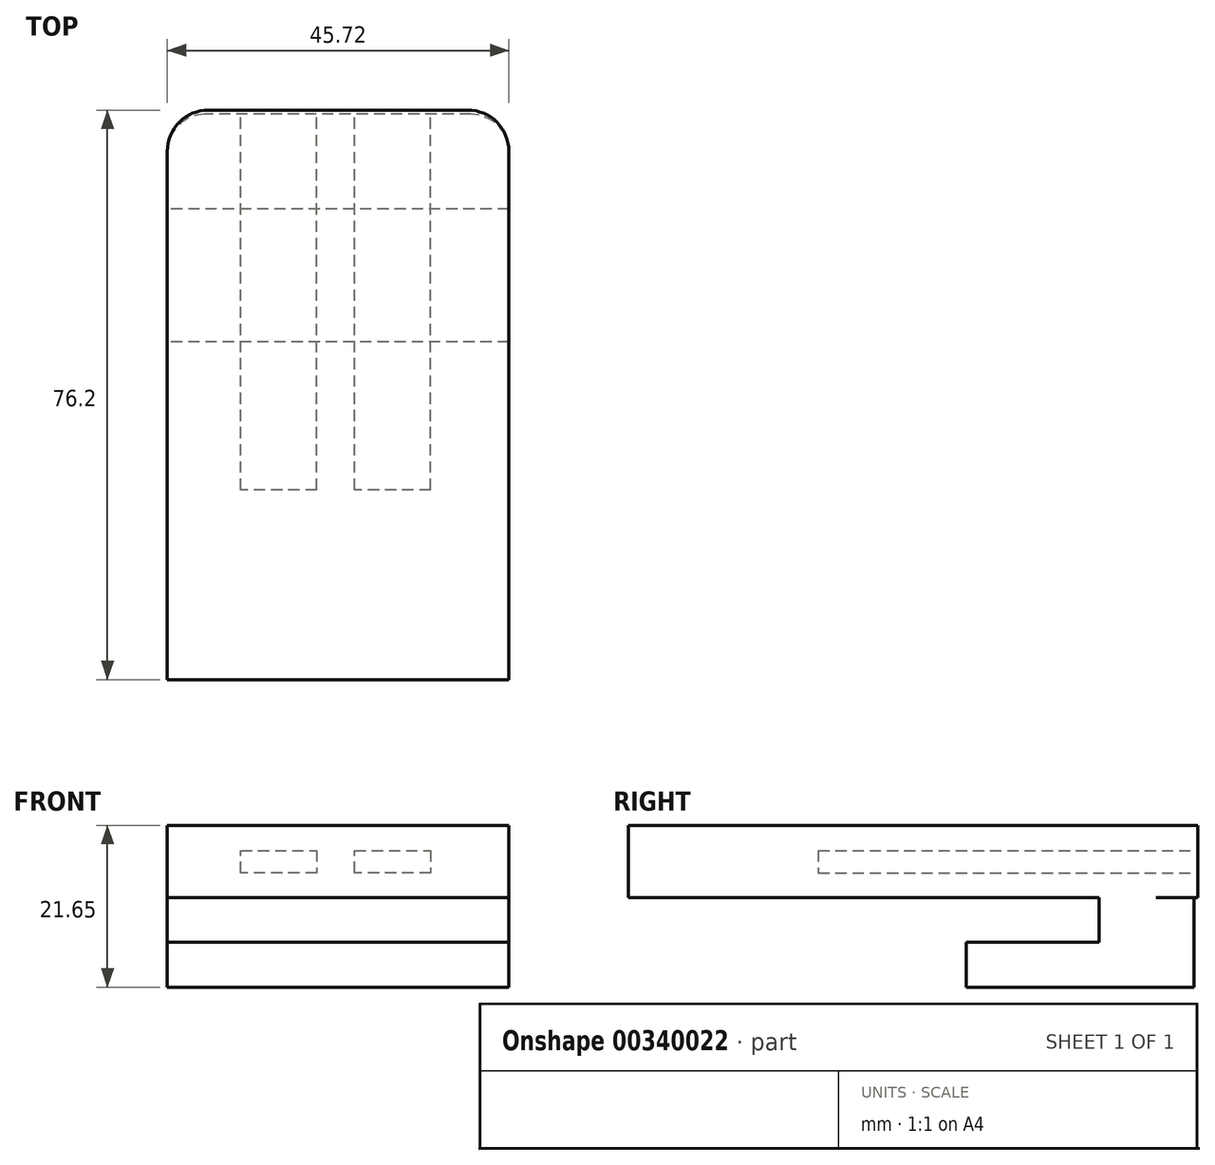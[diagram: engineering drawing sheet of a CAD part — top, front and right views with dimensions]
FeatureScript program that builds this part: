
annotation { "Feature Type Name" : "Feature", "Feature Type Description" : "" }
export const myFeature = defineFeature(function(context is Context, id is Id, definition is map)
    precondition{}
    {
        {
            var Q0;
            Q0=qCreatedBy(makeId("Top.planeOp"),FACE);
            var sketch = newSketch(context, id + "F0", { "sketchPlane" : qUnion([Q0])});
            skLineSegment(sketch, "E0", {"start": v(0, 0) * mm, "end": v(0, 13.65) * mm});
            skLineSegment(sketch, "E1", {"start": v(0, 0) * mm, "end": v(0, -62.55) * mm});
            skLineSegment(sketch, "E2", {"start": v(0, -62.55) * mm, "end": v(45.72, -62.55) * mm});
            skLineSegment(sketch, "E3", {"start": v(45.72, -62.55) * mm, "end": v(45.72, 13.65) * mm});
            skLineSegment(sketch, "E4", {"start": v(45.72, 13.65) * mm, "end": v(0, 13.65) * mm});
            skSolve(sketch);
        }
        {
            var Q0;
            Q0 = qSketchRegion(id + "F0", true);
            extrude(context, id + "F1", {"entities" : qUnion([Q0]), "depth" : 9.65 * mm});
        }
        {
            var Q0;
            Q0=qCreatedBy(makeId("Top.planeOp"),FACE);
            var sketch = newSketch(context, id + "F2", { "sketchPlane" : qUnion([Q0])});
            skLineSegment(sketch, "E5", {"start": v(0, 0) * mm, "end": v(0, 51.2) * mm});
            skLineSegment(sketch, "E6", {"start": v(0, 51.2) * mm, "end": v(0, -25) * mm});
            skLineSegment(sketch, "E7", {"start": v(0, -25) * mm, "end": v(45.72, -25) * mm});
            skLineSegment(sketch, "E8", {"start": v(45.72, -25) * mm, "end": v(45.72, 51.56) * mm});
            skLineSegment(sketch, "E9", {"start": v(45.72, 51.56) * mm, "end": v(0, 51.2) * mm});
            skSolve(sketch);
        }
        {
            var Q0;
            Q0=qCreatedBy(makeId("Right.planeOp"),FACE);
            var sketch = newSketch(context, id + "F3", { "sketchPlane" : qUnion([Q0])});
            skLineSegment(sketch, "E10", {"start": v(13.1, 0) * mm, "end": v(13.1, -12) * mm});
            skPoint(sketch, "E11.endSnap0", {"position": v(13.1, -6) * mm});
            skLineSegment(sketch, "E12", {"start": v(-17.38, -6) * mm, "end": v(0.4, -6) * mm});
            skLineSegment(sketch, "E13", {"start": v(0.4, -6) * mm, "end": v(0.4, 0) * mm});
            skLineSegment(sketch, "E14", {"start": v(13.1, 0) * mm, "end": v(0.4, 0) * mm});
            skLineSegment(sketch, "E15", {"start": v(13.1, -12) * mm, "end": v(-17.38, -12) * mm});
            skLineSegment(sketch, "E16", {"start": v(-17.38, -6) * mm, "end": v(-17.38, -12) * mm});
            skSolve(sketch);
        }
        {
            var Q0;
            Q0 = qSketchRegion(id + "F3", true);
            extrude(context, id + "F4", {"entities" : qUnion([Q0]), "operationType" : NewBodyOperationType.ADD, "depth" : 45.72 * mm});
        }
        {
            var Q0;
            Q0=makeQuery(id+"F4.opExtrude","CAP_EDGE",EDGE,{"disambiguationData":[OSD([sQuery(id+"F3.wireOp",EDGE,"E10")])],"isStart":false});
            var Q1;
            Q1=makeQuery(id+"F4.opExtrude","CAP_EDGE",EDGE,{"disambiguationData":[OSD([sQuery(id+"F3.wireOp",EDGE,"E10")])],"isStart":true});
            fillet(context, id + "F5", {"entities" : qUnion([Q0, Q1]), "radius" : 5.08 * mm, "tangentPropagation" : true, "allowEdgeOverflow" : false});
        }
        {
            var Q0;
            Q0=makeQuery(id+"F1.opExtrude","SWEPT_EDGE",EDGE,{"disambiguationData":[OSD([sQuery(id+"F0.wireOp",EDGE,"E3"),sQuery(id+"F0.wireOp",EDGE,"E4")])]});
            var Q1;
            Q1=makeQuery(id+"F1.opExtrude","SWEPT_EDGE",EDGE,{"disambiguationData":[OSD([sQuery(id+"F0.wireOp",EDGE,"E0"),sQuery(id+"F0.wireOp",EDGE,"E4")])]});
            fillet(context, id + "F6", {"entities" : qUnion([Q0, Q1]), "radius" : 5.52 * mm, "tangentPropagation" : true, "allowEdgeOverflow" : false});
        }
        {
            var Q0;
            Q0=makeQuery(id+"F1.opExtrude","SWEPT_FACE",FACE,{"disambiguationData":[OSD([sQuery(id+"F0.wireOp",EDGE,"E4")])]});
            var sketch = newSketch(context, id + "F7", { "sketchPlane" : qUnion([Q0])});
            skLineSegment(sketch, "E17", {"start": v(-35.24, 3.28) * mm, "end": v(-25.08, 3.28) * mm});
            skLineSegment(sketch, "E18", {"start": v(-25.08, 3.28) * mm, "end": v(-25.08, 6.28) * mm});
            skLineSegment(sketch, "E19", {"start": v(-25.08, 6.28) * mm, "end": v(-35.24, 6.28) * mm});
            skLineSegment(sketch, "E20", {"start": v(-35.24, 6.28) * mm, "end": v(-35.24, 3.28) * mm});
            skLineSegment(sketch, "E21", {"start": v(-20, 3.28) * mm, "end": v(-9.84, 3.28) * mm});
            skLineSegment(sketch, "E22", {"start": v(-9.84, 3.28) * mm, "end": v(-9.84, 6.28) * mm});
            skLineSegment(sketch, "E23", {"start": v(-9.84, 6.28) * mm, "end": v(-20, 6.28) * mm});
            skLineSegment(sketch, "E24", {"start": v(-20, 6.28) * mm, "end": v(-20, 3.28) * mm});
            skSolve(sketch);
        }
        {
            var Q0;
            Q0 = qSketchRegion(id + "F7", true);
            extrude(context, id + "F8", {"entities" : qUnion([Q0]), "operationType" : NewBodyOperationType.REMOVE, "oppositeDirection" : true, "depth" : 50.8 * mm});
        }
    });
